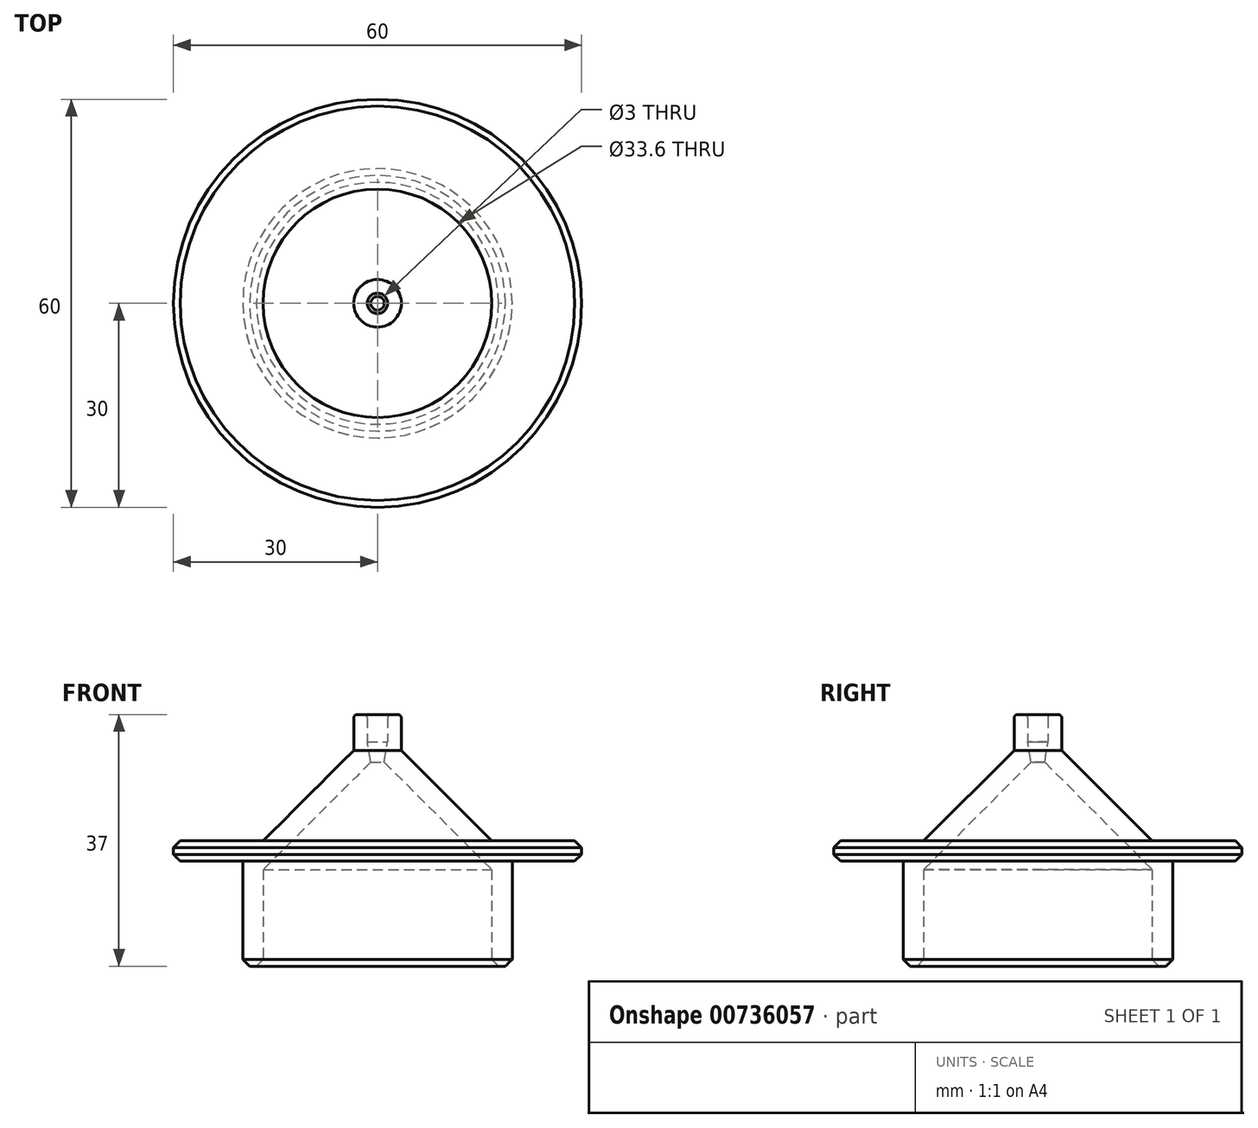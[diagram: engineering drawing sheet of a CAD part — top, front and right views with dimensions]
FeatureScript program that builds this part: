
annotation { "Feature Type Name" : "Feature", "Feature Type Description" : "" }
export const myFeature = defineFeature(function(context is Context, id is Id, definition is map)
    precondition{}
    {
        {
            var Q0;
            Q0=qCreatedBy(makeId("Front.planeOp"),FACE);
            var sketch = newSketch(context, id + "F0", { "sketchPlane" : qUnion([Q0])});
            skLineSegment(sketch, "E0", {"start": v(0, 0) * mm, "end": v(0, 70) * mm, "construction": true});
            skLineSegment(sketch, "E1", {"start": v(-19.8, 0) * mm, "end": v(-16.8, 0) * mm});
            skLineSegment(sketch, "E2", {"start": v(-16.8, 0) * mm, "end": v(-16.8, 14.2) * mm});
            skLineSegment(sketch, "E3", {"start": v(-16.8, 14.2) * mm, "end": v(-1, 30) * mm});
            skLineSegment(sketch, "E4", {"start": v(-3.5, 37) * mm, "end": v(-1.5, 37) * mm});
            skLineSegment(sketch, "E5", {"start": v(-1.5, 37) * mm, "end": v(-1.5, 33) * mm});
            skLineSegment(sketch, "E6", {"start": v(-1.5, 33) * mm, "end": v(-1, 30) * mm});
            skLineSegment(sketch, "E7", {"start": v(-3.5, 31.74) * mm, "end": v(-16.8, 18.44) * mm});
            skLineSegment(sketch, "E8", {"start": v(-19.8, 0) * mm, "end": v(-19.8, 15.44) * mm});
            skLineSegment(sketch, "E9", {"start": v(-3.5, 37) * mm, "end": v(-3.5, 31.74) * mm});
            skLineSegment(sketch, "E10", {"start": v(-19.8, 15.44) * mm, "end": v(-30, 15.44) * mm});
            skLineSegment(sketch, "E11", {"start": v(-30, 15.44) * mm, "end": v(-30, 18.44) * mm});
            skLineSegment(sketch, "E12", {"start": v(-30, 18.44) * mm, "end": v(-16.8, 18.44) * mm});
            skSolve(sketch);
        }
        {
            var Q0;
            Q0 = qSketchRegion(id + "F0", true);
            var Q1;
            Q1=sQuery(id+"F0.wireOp",EDGE,"E0");
            revolve(context, id + "F1", {"surfaceOperationType" : NewSurfaceOperationType.NEW, "entities" : qUnion([Q0]), "axis" : qUnion([Q1]), "revolveType" : RevolveType.FULL});
        }
        {
            var Q0;
            Q0=makeQuery(id+"F1.opRevolve","SWEPT_EDGE",EDGE,{"disambiguationData":[OSD([sQuery(id+"F0.wireOp",EDGE,"E1"),sQuery(id+"F0.wireOp",EDGE,"tCUR60Xb-deOk-wKAM-x0km-w9TfkZSNbDSF")])]});
            var Q1;
            Q1=makeQuery(id+"F1.opRevolve","SWEPT_EDGE",EDGE,{"disambiguationData":[OSD([sQuery(id+"F0.wireOp",EDGE,"8qVdnP3X-cWQH-McHR-B2hm-MtRxavH2fmOx"),sQuery(id+"F0.wireOp",EDGE,"7cLS4jYQ-BhFO-Ymm0-LkvB-nA02IeAbKdVi")])]});
            var Q2;
            Q2=makeQuery(id+"F1.opRevolve","SWEPT_EDGE",EDGE,{"disambiguationData":[OSD([sQuery(id+"F0.wireOp",EDGE,"E11"),sQuery(id+"F0.wireOp",EDGE,"E12")])]});
            var Q3;
            Q3=makeQuery(id+"F1.opRevolve","SWEPT_EDGE",EDGE,{"disambiguationData":[OSD([sQuery(id+"F0.wireOp",EDGE,"E10"),sQuery(id+"F0.wireOp",EDGE,"E11")])]});
            chamfer(context, id + "F2", {"entities" : qUnion([Q0, Q1, Q2, Q3]), "width" : 1 * mm, "tangentPropagation" : true});
        }
        {
            var Q0;
            Q0=makeQuery(id+"F1.opRevolve","SWEPT_EDGE",EDGE,{"disambiguationData":[OSD([sQuery(id+"F0.wireOp",EDGE,"E4"),sQuery(id+"F0.wireOp",EDGE,"E5")])]});
            var Q1;
            Q1=makeQuery(id+"F1.opRevolve","SWEPT_EDGE",EDGE,{"disambiguationData":[OSD([sQuery(id+"F0.wireOp",EDGE,"E4"),sQuery(id+"F0.wireOp",EDGE,"5tgoNkw9-v3yP-iS7n-kMiK-30jeHwsuH2La")])]});
            var Q2;
            Q2=makeQuery(id+"F1.opRevolve","SWEPT_EDGE",EDGE,{"disambiguationData":[OSD([sQuery(id+"F0.wireOp",EDGE,"5Rbltm6K-41DU-C12r-f2bn-UkiEKg5Jt9Vl"),sQuery(id+"F0.wireOp",EDGE,"FKnxS3HQ-xS4U-L6uY-TZS3-us5KEXquMp8L")])]});
            fillet(context, id + "F3", {"entities" : qUnion([Q0, Q1, Q2]), "radius" : .5 * mm, "tangentPropagation" : true, "allowEdgeOverflow" : false});
        }
    });
